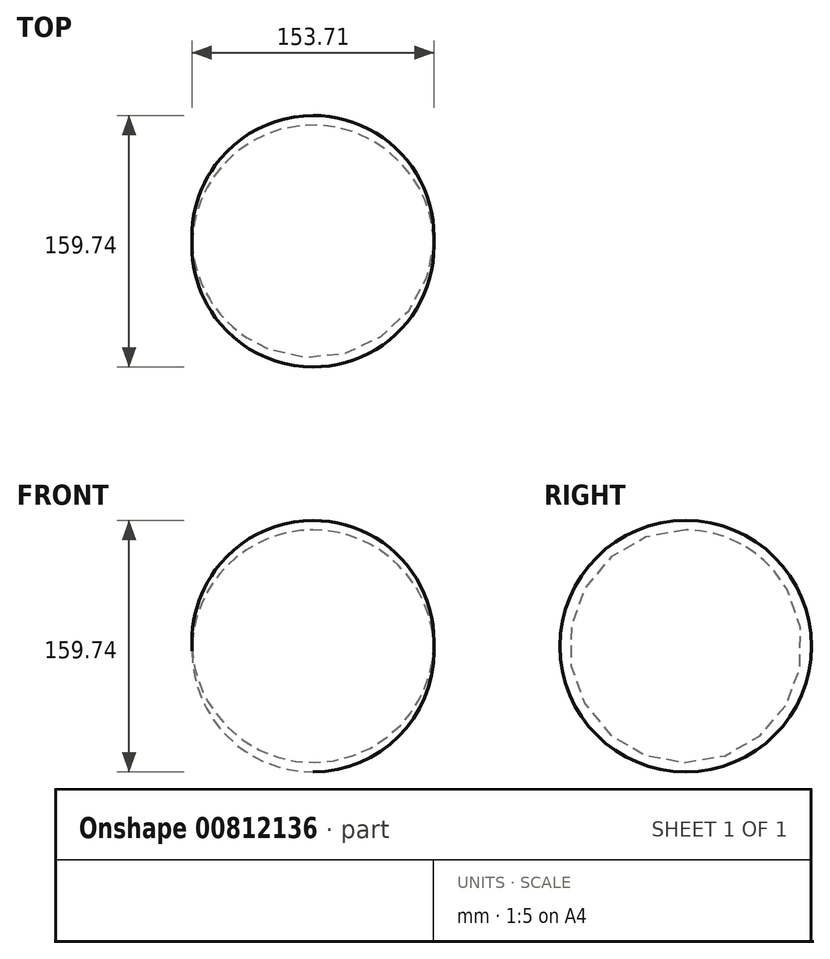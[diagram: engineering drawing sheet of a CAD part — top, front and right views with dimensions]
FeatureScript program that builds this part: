
annotation { "Feature Type Name" : "Feature", "Feature Type Description" : "" }
export const myFeature = defineFeature(function(context is Context, id is Id, definition is map)
    precondition{}
    {
        {
            var Q0;
            Q0=qCreatedBy(makeId("Top.planeOp"),FACE);
            var sketch = newSketch(context, id + "F0", { "sketchPlane" : qUnion([Q0])});
            skLineSegment(sketch, "E0", {"start": v(0, 0) * mm, "end": v(153.6, 0) * mm});
            skArc(sketch, "E1", {"start": v(153.6, 0) * mm, "mid": v(76.8, 73.84) * mm, "end": v(0, 0) * mm});
            skSolve(sketch);
        }
        {
            var Q0;
            Q0=makeQuery(id+"F0.imprint","IMPRINT",FACE,{"disambiguationData":[TD([[makeQuery(id+"F0.imprint","IMPRINT",EDGE,{"derivedFrom":sQuery(id+"F0.wireOp",EDGE,"E0")}),1.0]])]});
            var Q1;
            Q1=sQuery(id+"F0.wireOp",EDGE,"E1");
            var Q2;
            Q2=sQuery(id+"F0.wireOp",EDGE,"E0");
            revolve(context, id + "F1", {"bodyType" : ToolBodyType.SURFACE, "surfaceOperationType" : NewSurfaceOperationType.NEW, "entities" : qUnion([Q0]), "surfaceEntities" : qUnion([Q1]), "axis" : qUnion([Q2]), "revolveType" : RevolveType.FULL});
        }
    });
